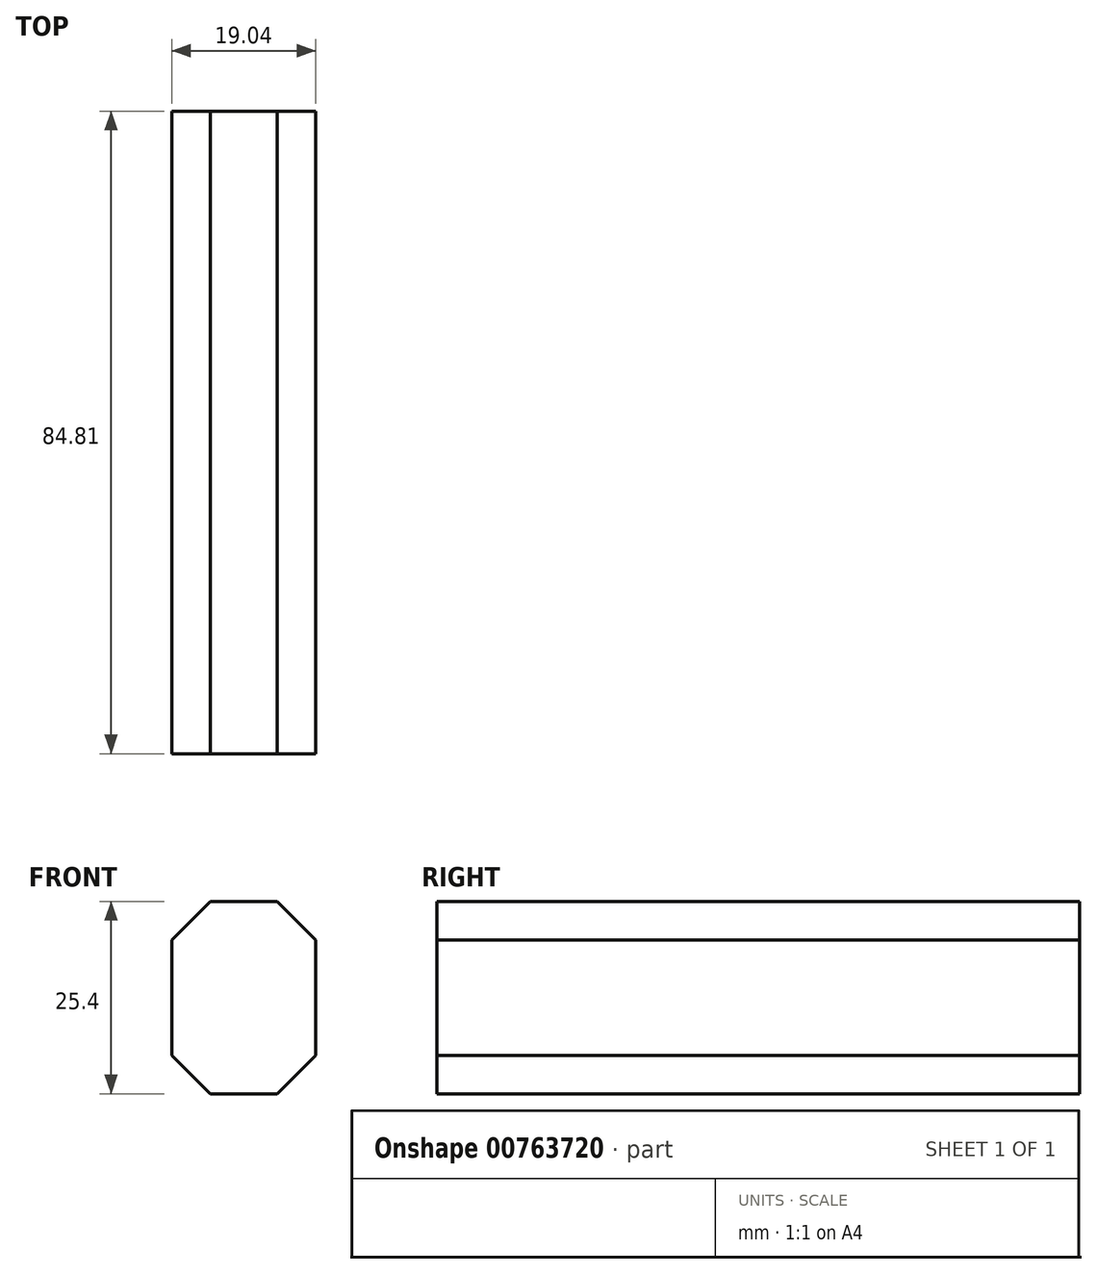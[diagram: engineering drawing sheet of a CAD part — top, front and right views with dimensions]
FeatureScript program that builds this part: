
annotation { "Feature Type Name" : "Feature", "Feature Type Description" : "" }
export const myFeature = defineFeature(function(context is Context, id is Id, definition is map)
    precondition{}
    {
        {
            var Q0;
            Q0=qCreatedBy(makeId("Top.planeOp"),FACE);
            var sketch = newSketch(context, id + "F0", { "sketchPlane" : qUnion([Q0])});
            skLineSegment(sketch, "E0.bottom", {"start": v(0, 0) * mm, "end": v(17.77, 0) * mm});
            skLineSegment(sketch, "E0.top", {"start": v(0, -42.3) * mm, "end": v(17.77, -42.3) * mm});
            skLineSegment(sketch, "E0.left", {"start": v(0, 0) * mm, "end": v(0, -42.3) * mm});
            skLineSegment(sketch, "E0.right", {"start": v(17.77, 0) * mm, "end": v(17.77, -42.3) * mm});
            skLineSegment(sketch, "E1.bottom", {"start": v(43.36, -42.3) * mm, "end": v(24.32, -42.3) * mm});
            skLineSegment(sketch, "E1.top", {"start": v(43.36, 42.51) * mm, "end": v(24.32, 42.51) * mm});
            skLineSegment(sketch, "E1.left", {"start": v(43.36, -42.3) * mm, "end": v(43.36, 42.51) * mm});
            skLineSegment(sketch, "E1.right", {"start": v(24.32, -42.3) * mm, "end": v(24.32, 42.51) * mm});
            skSolve(sketch);
        }
        {
            var Q0;
            Q0=makeQuery(id+"F0.imprint","IMPRINT",FACE,{"disambiguationData":[TD([[makeQuery(id+"F0.imprint","IMPRINT",EDGE,{"derivedFrom":sQuery(id+"F0.wireOp",EDGE,"E1.bottom")}),-1.0]])]});
            extrude(context, id + "F1", {"entities" : qUnion([Q0]), "depth" : 25.4 * mm, "offsetDistance" : 25.4 * mm});
        }
        {
            var Q0;
            Q0=makeQuery(id+"F1.opExtrude","CAP_EDGE",EDGE,{"disambiguationData":[OSD([sQuery(id+"F0.wireOp",EDGE,"E1.right")])],"isStart":true});
            var Q1;
            Q1=makeQuery(id+"F1.opExtrude","CAP_EDGE",EDGE,{"disambiguationData":[OSD([sQuery(id+"F0.wireOp",EDGE,"E1.right")])],"isStart":false});
            var Q2;
            Q2=makeQuery(id+"F1.opExtrude","CAP_EDGE",EDGE,{"disambiguationData":[OSD([sQuery(id+"F0.wireOp",EDGE,"E1.left")])],"isStart":true});
            var Q3;
            Q3=makeQuery(id+"F1.opExtrude","CAP_EDGE",EDGE,{"disambiguationData":[OSD([sQuery(id+"F0.wireOp",EDGE,"E1.left")])],"isStart":false});
            chamfer(context, id + "F2", {"entities" : qUnion([Q0, Q1, Q2, Q3]), "width" : 5.08 * mm, "tangentPropagation" : true});
        }
    });
